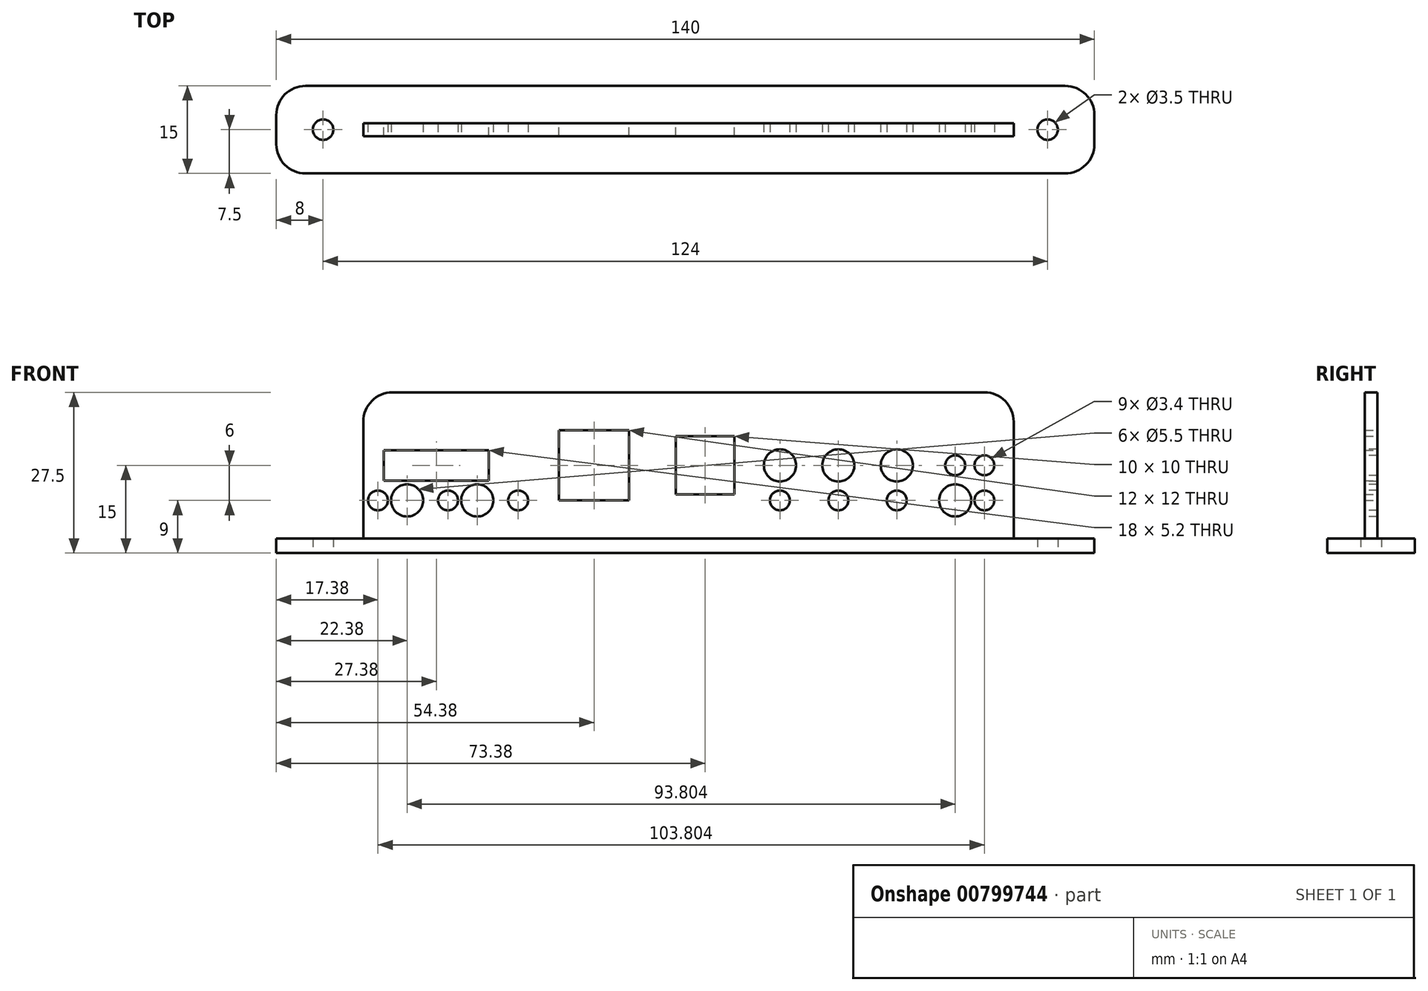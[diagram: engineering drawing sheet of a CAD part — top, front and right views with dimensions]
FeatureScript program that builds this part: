
annotation { "Feature Type Name" : "Feature", "Feature Type Description" : "" }
export const myFeature = defineFeature(function(context is Context, id is Id, definition is map)
    precondition{}
    {
        {
            var Q0;
            Q0=qCreatedBy(makeId("Top.planeOp"),FACE);
            var sketch = newSketch(context, id + "F0", { "sketchPlane" : qUnion([Q0])});
            skLineSegment(sketch, "E0.bottom", {"start": v(70, -7.5) * mm, "end": v(-70, -7.5) * mm});
            skLineSegment(sketch, "E0.top", {"start": v(70, 7.5) * mm, "end": v(-70, 7.5) * mm});
            skLineSegment(sketch, "E0.left", {"start": v(70, -7.5) * mm, "end": v(70, 7.5) * mm});
            skLineSegment(sketch, "E0.right", {"start": v(-70, -7.5) * mm, "end": v(-70, 7.5) * mm});
            skPoint(sketch, "E0.middle", {"position": v(0, 0) * mm});
            skPoint(sketch, "E1", {"position": v(-62, 0) * mm});
            skPoint(sketch, "E2", {"position": v(62, 0) * mm});
            skCircle(sketch, "E3", {"center": v(-62, 0) * mm, "radius": 1.75 * mm});
            skCircle(sketch, "E4", {"center": v(62, 0) * mm, "radius": 1.75 * mm});
            skSolve(sketch);
        }
        {
            var Q0;
            Q0=makeQuery(id+"F0.imprint","IMPRINT",FACE,{"disambiguationData":[TD([[makeQuery(id+"F0.imprint","IMPRINT",EDGE,{"derivedFrom":sQuery(id+"F0.wireOp",EDGE,"E0.bottom")}),-1.0]])]});
            extrude(context, id + "F1", {"entities" : qUnion([Q0]), "depth" : 2.5 * mm, "offsetDistance" : 25 * mm});
        }
        {
            var Q0;
            Q0=makeQuery(id+"F1.opExtrude","CAP_FACE",FACE,{"disambiguationData":[OSD([sQuery(id+"F0.wireOp",EDGE,"E0.bottom"),sQuery(id+"F0.wireOp",EDGE,"E0.top"),sQuery(id+"F0.wireOp",EDGE,"E0.left"),sQuery(id+"F0.wireOp",EDGE,"E0.right"),sQuery(id+"F0.wireOp",EDGE,"E3"),sQuery(id+"F0.wireOp",EDGE,"E4")])],"isStart":false});
            var sketch = newSketch(context, id + "F2", { "sketchPlane" : qUnion([Q0])});
            skPoint(sketch, "E5", {"position": v(-55.12, 0) * mm});
            skPoint(sketch, "E6", {"position": v(56.18, 0) * mm});
            skPoint(sketch, "E7", {"position": v(56.18, 1.1) * mm});
            skPoint(sketch, "E8", {"position": v(56.18, -1.1) * mm});
            skPoint(sketch, "E9", {"position": v(-55.12, -1.1) * mm});
            skPoint(sketch, "E10", {"position": v(-55.12, 1.1) * mm});
            skLineSegment(sketch, "E11", {"start": v(-55.12, 1.1) * mm, "end": v(56.18, 1.1) * mm});
            skLineSegment(sketch, "E12", {"start": v(56.18, 1.1) * mm, "end": v(56.18, 0) * mm});
            skLineSegment(sketch, "E13", {"start": v(56.18, -1.1) * mm, "end": v(-55.12, -1.1) * mm});
            skLineSegment(sketch, "E14", {"start": v(-55.12, -1.1) * mm, "end": v(-55.12, 1.1) * mm});
            skLineSegment(sketch, "E15", {"start": v(56.18, 0) * mm, "end": v(56.18, -1.1) * mm});
            skSolve(sketch);
        }
        {
            var Q0;
            Q0=makeQuery(id+"F2.imprint","IMPRINT",FACE,{"disambiguationData":[TD([[makeQuery(id+"F2.imprint","IMPRINT",EDGE,{"derivedFrom":sQuery(id+"F2.wireOp",EDGE,"E11")}),-1.0]])]});
            extrude(context, id + "F3", {"entities" : qUnion([Q0]), "operationType" : NewBodyOperationType.ADD, "depth" : 25 * mm, "offsetDistance" : 25 * mm});
        }
        {
            var Q0;
            Q0=makeQuery(id+"F3.opExtrude","SWEPT_FACE",FACE,{"disambiguationData":[OSD([sQuery(id+"F2.wireOp",EDGE,"E11")])]});
            var sketch = newSketch(context, id + "F4", { "sketchPlane" : qUnion([Q0])});
            skPoint(sketch, "E16", {"position": v(-56.18, 15) * mm});
            skPoint(sketch, "E17", {"position": v(55.12, 15) * mm});
            skLineSegment(sketch, "E18", {"start": v(-56.18, 15) * mm, "end": v(55.12, 15) * mm});
            skPoint(sketch, "E19", {"position": v(-51.18, 15) * mm});
            skPoint(sketch, "E20", {"position": v(-46.18, 15) * mm});
            skPoint(sketch, "E21", {"position": v(-36.18, 15) * mm});
            skPoint(sketch, "E22", {"position": v(-26.18, 15) * mm});
            skPoint(sketch, "E23", {"position": v(-16.18, 15) * mm});
            skPoint(sketch, "E24", {"position": v(51.62, 15) * mm});
            skPoint(sketch, "E25", {"position": v(51.62, 17.6) * mm});
            skPoint(sketch, "E26", {"position": v(51.62, 12.4) * mm});
            skPoint(sketch, "E27", {"position": v(33.62, 12.4) * mm});
            skPoint(sketch, "E28", {"position": v(33.62, 17.6) * mm});
            skLineSegment(sketch, "E29", {"start": v(33.62, 17.6) * mm, "end": v(51.62, 17.6) * mm});
            skLineSegment(sketch, "E30", {"start": v(51.62, 17.6) * mm, "end": v(51.62, 12.4) * mm});
            skLineSegment(sketch, "E31", {"start": v(51.62, 12.4) * mm, "end": v(33.62, 12.4) * mm});
            skLineSegment(sketch, "E32", {"start": v(33.62, 12.4) * mm, "end": v(33.62, 17.6) * mm});
            skPoint(sketch, "E33", {"position": v(21.62, 15) * mm});
            skPoint(sketch, "E34", {"position": v(21.62, 21) * mm});
            skPoint(sketch, "E35", {"position": v(21.62, 9) * mm});
            skPoint(sketch, "E36", {"position": v(9.62, 9) * mm});
            skPoint(sketch, "E37", {"position": v(9.62, 21) * mm});
            skLineSegment(sketch, "E38", {"start": v(9.62, 21) * mm, "end": v(21.62, 21) * mm});
            skLineSegment(sketch, "E39", {"start": v(21.62, 21) * mm, "end": v(21.62, 9) * mm});
            skLineSegment(sketch, "E40", {"start": v(21.62, 9) * mm, "end": v(9.62, 9) * mm});
            skLineSegment(sketch, "E41", {"start": v(9.62, 9) * mm, "end": v(9.62, 21) * mm});
            skPoint(sketch, "E42", {"position": v(1.62, 15) * mm});
            skPoint(sketch, "E43", {"position": v(1.62, 20) * mm});
            skPoint(sketch, "E44", {"position": v(1.62, 10) * mm});
            skPoint(sketch, "E45", {"position": v(-8.38, 10) * mm});
            skPoint(sketch, "E46", {"position": v(-8.38, 20) * mm});
            skLineSegment(sketch, "E47", {"start": v(-8.38, 20) * mm, "end": v(1.62, 20) * mm});
            skLineSegment(sketch, "E48", {"start": v(1.62, 20) * mm, "end": v(1.62, 10) * mm});
            skLineSegment(sketch, "E49", {"start": v(1.62, 10) * mm, "end": v(-8.38, 10) * mm});
            skLineSegment(sketch, "E50", {"start": v(-8.38, 10) * mm, "end": v(-8.38, 20) * mm});
            skPoint(sketch, "E51", {"position": v(-16.18, 9) * mm});
            skPoint(sketch, "E52", {"position": v(-26.18, 9) * mm});
            skPoint(sketch, "E53", {"position": v(-36.18, 9) * mm});
            skPoint(sketch, "E54", {"position": v(-46.18, 9) * mm});
            skPoint(sketch, "E55", {"position": v(-51.18, 9) * mm});
            skPoint(sketch, "E56", {"position": v(28.62, 9) * mm});
            skPoint(sketch, "E57", {"position": v(35.62, 9) * mm});
            skPoint(sketch, "E58", {"position": v(40.62, 9) * mm});
            skPoint(sketch, "E59", {"position": v(47.62, 9) * mm});
            skPoint(sketch, "E60", {"position": v(52.62, 9) * mm});
            skSolve(sketch);
        }
        {
            var Q0;
            {var subQ5=sQuery(id+"F4.wireOp",EDGE,"E29");Q0=makeQuery(id+"F4.imprint","IMPRINT",FACE,{"disambiguationData":[TD([[makeQuery(id+"F4.imprint","IMPRINT",EDGE,{"derivedFrom":subQ5}),-1.0]])]});}
            var Q1;
            {var subQ5=sQuery(id+"F4.wireOp",EDGE,"E31");Q1=makeQuery(id+"F4.imprint","IMPRINT",FACE,{"disambiguationData":[TD([[makeQuery(id+"F4.imprint","IMPRINT",EDGE,{"derivedFrom":subQ5}),-1.0]])]});}
            var Q2;
            {var subQ5=sQuery(id+"F4.wireOp",EDGE,"E38");Q2=makeQuery(id+"F4.imprint","IMPRINT",FACE,{"disambiguationData":[TD([[makeQuery(id+"F4.imprint","IMPRINT",EDGE,{"derivedFrom":subQ5}),-1.0]])]});}
            var Q3;
            {var subQ5=sQuery(id+"F4.wireOp",EDGE,"E40");Q3=makeQuery(id+"F4.imprint","IMPRINT",FACE,{"disambiguationData":[TD([[makeQuery(id+"F4.imprint","IMPRINT",EDGE,{"derivedFrom":subQ5}),-1.0]])]});}
            var Q4;
            {var subQ5=sQuery(id+"F4.wireOp",EDGE,"E47");Q4=makeQuery(id+"F4.imprint","IMPRINT",FACE,{"disambiguationData":[TD([[makeQuery(id+"F4.imprint","IMPRINT",EDGE,{"derivedFrom":subQ5}),-1.0]])]});}
            var Q5;
            {var subQ5=sQuery(id+"F4.wireOp",EDGE,"E49");Q5=makeQuery(id+"F4.imprint","IMPRINT",FACE,{"disambiguationData":[TD([[makeQuery(id+"F4.imprint","IMPRINT",EDGE,{"derivedFrom":subQ5}),-1.0]])]});}
            extrude(context, id + "F5", {"entities" : qUnion([Q0, Q1, Q2, Q3, Q4, Q5]), "operationType" : NewBodyOperationType.REMOVE, "oppositeDirection" : true, "depth" : 25 * mm, "offsetDistance" : 25 * mm});
        }
        {
            var Q0;
            Q0=sQuery(id+"F4.wireOp",VERTEX,"E19");
            var Q1;
            Q1=sQuery(id+"F4.wireOp",VERTEX,"E20");
            var Q2;
            Q2=sQuery(id+"F4.wireOp",VERTEX,"E51");
            var Q3;
            Q3=sQuery(id+"F4.wireOp",VERTEX,"E52");
            var Q4;
            Q4=sQuery(id+"F4.wireOp",VERTEX,"E53");
            var Q5;
            Q5=sQuery(id+"F4.wireOp",VERTEX,"E55");
            var Q6;
            Q6=sQuery(id+"F4.wireOp",VERTEX,"E60");
            var Q7;
            Q7=sQuery(id+"F4.wireOp",VERTEX,"E58");
            var Q8;
            Q8=sQuery(id+"F4.wireOp",VERTEX,"E56");
            var Q9;
            Q9=makeQuery(id+"F1.opExtrude","SWEPT_BODY",BODY,{"disambiguationData":[OSD([sQuery(id+"F0.wireOp",EDGE,"E0.bottom"),sQuery(id+"F0.wireOp",EDGE,"E0.top"),sQuery(id+"F0.wireOp",EDGE,"E0.left"),sQuery(id+"F0.wireOp",EDGE,"E0.right"),sQuery(id+"F0.wireOp",EDGE,"E3"),sQuery(id+"F0.wireOp",EDGE,"E4")])]});
            hole(context, id + "F6", {"style" : HoleStyle.SIMPLE, "endStyle" : HoleEndStyle.THROUGH, "standardTappedOrClearance" : lookupTablePath({ "fit" : "Normal", "standard" : "ISO", "size" : "M3", "type" : "Clearance" }), "standardBlindInLast" : lookupTablePath({ "fit" : "Normal", "standard" : "ISO", "engagement" : "75%", "pitch" : "0.5 mm", "size" : "M3", "type" : "Clearance & tapped" }), "holeDiameter" : 3.4 * mm, "majorDiameter" : 5 * mm, "isTappedThrough" : true, "tappedDepth" : 12 * mm, "tapClearance" : 3, "startFromSketch" : true, "locations" : qUnion([Q0, Q1, Q2, Q3, Q4, Q5, Q6, Q7, Q8]), "scope" : qUnion([Q9])});
        }
        {
            var Q0;
            Q0=sQuery(id+"F4.wireOp",VERTEX,"E21");
            var Q1;
            Q1=sQuery(id+"F4.wireOp",VERTEX,"E22");
            var Q2;
            Q2=sQuery(id+"F4.wireOp",VERTEX,"E23");
            var Q3;
            Q3=sQuery(id+"F4.wireOp",VERTEX,"E54");
            var Q4;
            Q4=sQuery(id+"F4.wireOp",VERTEX,"E59");
            var Q5;
            Q5=sQuery(id+"F4.wireOp",VERTEX,"E57");
            var Q6;
            Q6=makeQuery(id+"F1.opExtrude","SWEPT_BODY",BODY,{"disambiguationData":[OSD([sQuery(id+"F0.wireOp",EDGE,"E0.bottom"),sQuery(id+"F0.wireOp",EDGE,"E0.top"),sQuery(id+"F0.wireOp",EDGE,"E0.left"),sQuery(id+"F0.wireOp",EDGE,"E0.right"),sQuery(id+"F0.wireOp",EDGE,"E3"),sQuery(id+"F0.wireOp",EDGE,"E4")])]});
            hole(context, id + "F7", {"style" : HoleStyle.SIMPLE, "endStyle" : HoleEndStyle.THROUGH, "standardTappedOrClearance" : lookupTablePath({ "fit" : "Normal", "standard" : "ISO", "size" : "M5", "type" : "Clearance" }), "standardBlindInLast" : lookupTablePath({ "fit" : "Normal", "standard" : "ISO", "engagement" : "75%", "pitch" : "0.8 mm", "size" : "M5", "type" : "Clearance & tapped" }), "holeDiameter" : 5.5 * mm, "majorDiameter" : 5 * mm, "isTappedThrough" : true, "tappedDepth" : 12 * mm, "tapClearance" : 3, "startFromSketch" : true, "locations" : qUnion([Q0, Q1, Q2, Q3, Q4, Q5]), "scope" : qUnion([Q6])});
        }
        {
            var Q0;
            Q0=makeQuery(id+"F3.opExtrude","CAP_EDGE",EDGE,{"disambiguationData":[OSD([sQuery(id+"F2.wireOp",EDGE,"E12"),sQuery(id+"F2.wireOp",EDGE,"E15")])],"isStart":false});
            var Q1;
            Q1=makeQuery(id+"F3.opExtrude","CAP_EDGE",EDGE,{"disambiguationData":[OSD([sQuery(id+"F2.wireOp",EDGE,"E14")])],"isStart":false});
            var Q2;
            Q2=makeQuery(id+"F1.opExtrude","SWEPT_EDGE",EDGE,{"disambiguationData":[OSD([sQuery(id+"F0.wireOp",EDGE,"E0.top"),sQuery(id+"F0.wireOp",EDGE,"E0.left")])]});
            var Q3;
            Q3=makeQuery(id+"F1.opExtrude","SWEPT_EDGE",EDGE,{"disambiguationData":[OSD([sQuery(id+"F0.wireOp",EDGE,"E0.bottom"),sQuery(id+"F0.wireOp",EDGE,"E0.left")])]});
            var Q4;
            Q4=makeQuery(id+"F1.opExtrude","SWEPT_EDGE",EDGE,{"disambiguationData":[OSD([sQuery(id+"F0.wireOp",EDGE,"E0.top"),sQuery(id+"F0.wireOp",EDGE,"E0.right")])]});
            var Q5;
            Q5=makeQuery(id+"F1.opExtrude","SWEPT_EDGE",EDGE,{"disambiguationData":[OSD([sQuery(id+"F0.wireOp",EDGE,"E0.bottom"),sQuery(id+"F0.wireOp",EDGE,"E0.right")])]});
            fillet(context, id + "F8", {"entities" : qUnion([Q0, Q1, Q2, Q3, Q4, Q5]), "tangentPropagation" : true, "radius" : 5 * mm, "defaultsChanged" : false, "vertexSettings" : [], "allowEdgeOverflow" : false});
        }
    });
